# Revit family: RAUPIANO PLUS Reducer
name_source: partatom
category: Pipe Fittings
revit_build: Autodesk Revit MEP 2012 (Build: 20110309_2315(x64)
units: mm (PartAtom-declared; Revit-internal decimal feet)

## types (1)
- Standard
    A1 = 123124-001
    A10 = 121804-002
    A11 = 123764-001
    A2 = 121384-001
    A3 = 123314-001
    A4 = 123324-001
    A5 = 121394-001
    A6 = 121404-001
    A7 = 121994-001
    A8 = 120614-001
    A9 = 124039-001
    Description = REHAU RAUPIANO PLUS reducer
    Fail = No article found
    Lookup Table Name = RAUPIANO Reducer.csv
    M1 = 11231241001
    M10 = 11218041002
    M11 = 11237641001
    M2 = 11213841001
    M3 = 11233141001
    M4 = 11233241001
    M5 = 11213941001
    M6 = 11214041001
    M7 = 11219941001
    M8 = 11206141001
    M9 = 11240391001
    Manufacturer = REHAU
    T1 = DN 50/40
    T10 = DN 160/125
    T11 = DN 200/160
    T2 = DN 75/50
    T3 = DN 90/50
    T4 = DN 90/75
    T5 = DN 110/50
    T6 = DN 110/75
    T7 = DN 110/90
    T8 = DN 125/110
    T9 = DN 160/110
    Type Comments = RAU-PP; Push-fit; White

## geometry (parser evidence)
native form markers: Sweep x4
no freeform markers — native parametric forms only
